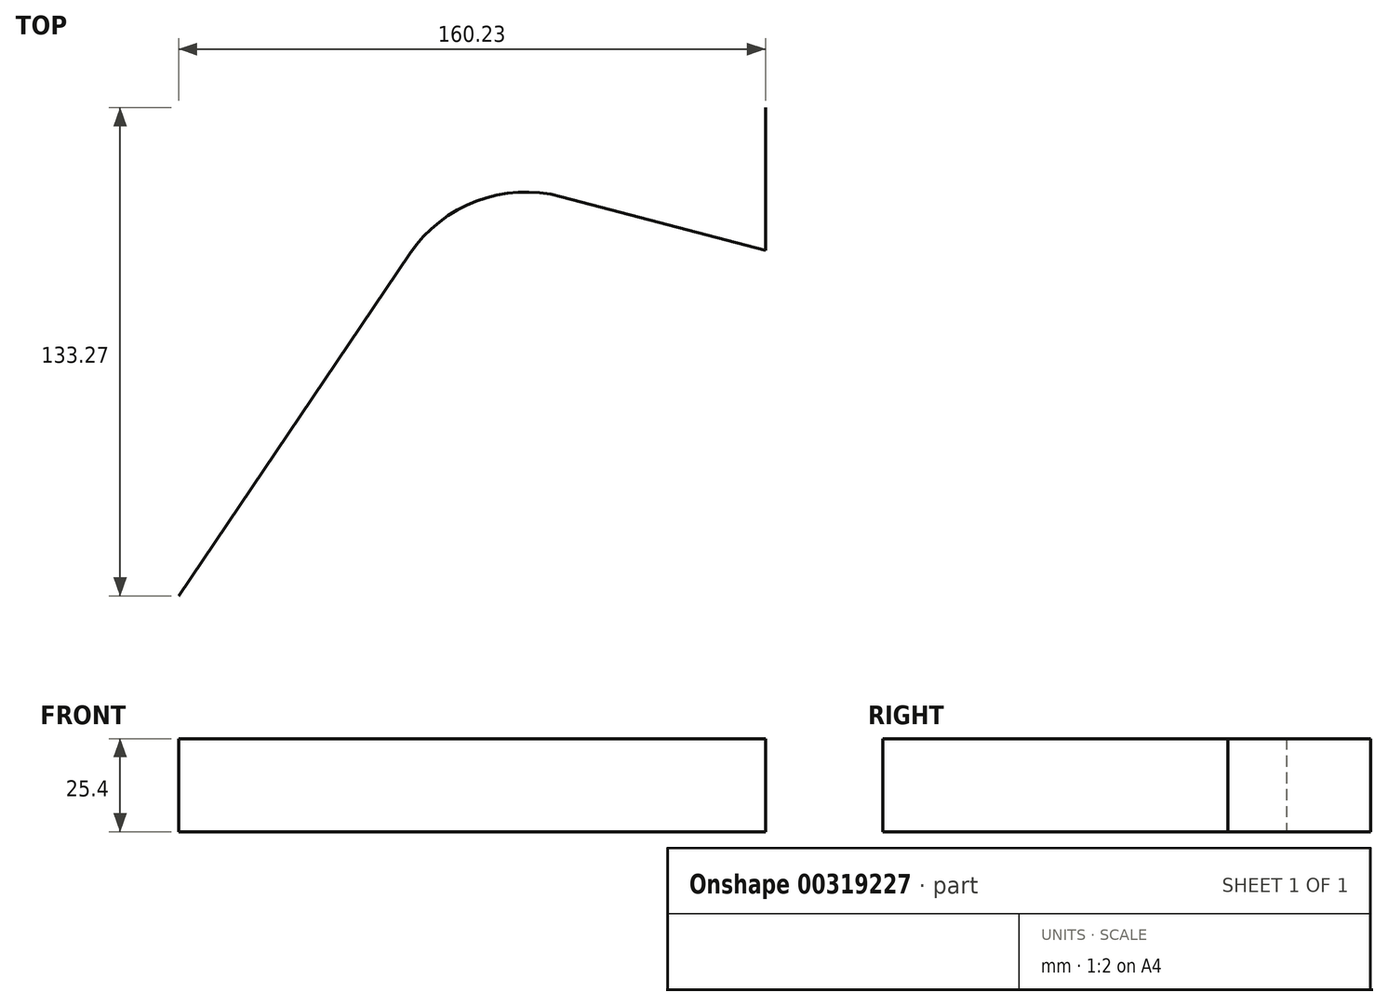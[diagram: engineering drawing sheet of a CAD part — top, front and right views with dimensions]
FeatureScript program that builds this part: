
annotation { "Feature Type Name" : "Feature", "Feature Type Description" : "" }
export const myFeature = defineFeature(function(context is Context, id is Id, definition is map)
    precondition{}
    {
        {
            var Q0;
            Q0=qCreatedBy(makeId("Top.planeOp"),FACE);
            var sketch = newSketch(context, id + "F0", { "sketchPlane" : qUnion([Q0])});
            skLineSegment(sketch, "E0", {"start": v(-109.7, -76.4) * mm, "end": v(-31.4, 39.47) * mm});
            skLineSegment(sketch, "E1", {"start": v(-31.4, 39.47) * mm, "end": v(50.54, 17.9) * mm});
            skLineSegment(sketch, "E2", {"start": v(50.54, 17.9) * mm, "end": v(50.54, 56.87) * mm});
            skSolve(sketch);
        }
        {
            var Q0;
            Q0=sQuery(id+"F0.wireOp",EDGE,"E0");
            var Q1;
            Q1=sQuery(id+"F0.wireOp",EDGE,"E1");
            var Q2;
            Q2=sQuery(id+"F0.wireOp",EDGE,"E2");
            extrude(context, id + "F1", {"bodyType" : ToolBodyType.SURFACE, "surfaceEntities" : qUnion([Q0, Q1, Q2]), "depth" : 25.4 * mm});
        }
        {
            var Q0;
            Q0=makeQuery(id+"F1.opExtrude","SWEPT_EDGE",EDGE,{"disambiguationData":[OSD([sQuery(id+"F0.wireOp",VERTEX,"E1.start")])]});
            fillet(context, id + "F2", {"entities" : qUnion([Q0]), "radius" : 38.2 * mm, "tangentPropagation" : true, "allowEdgeOverflow" : false});
        }
    });
